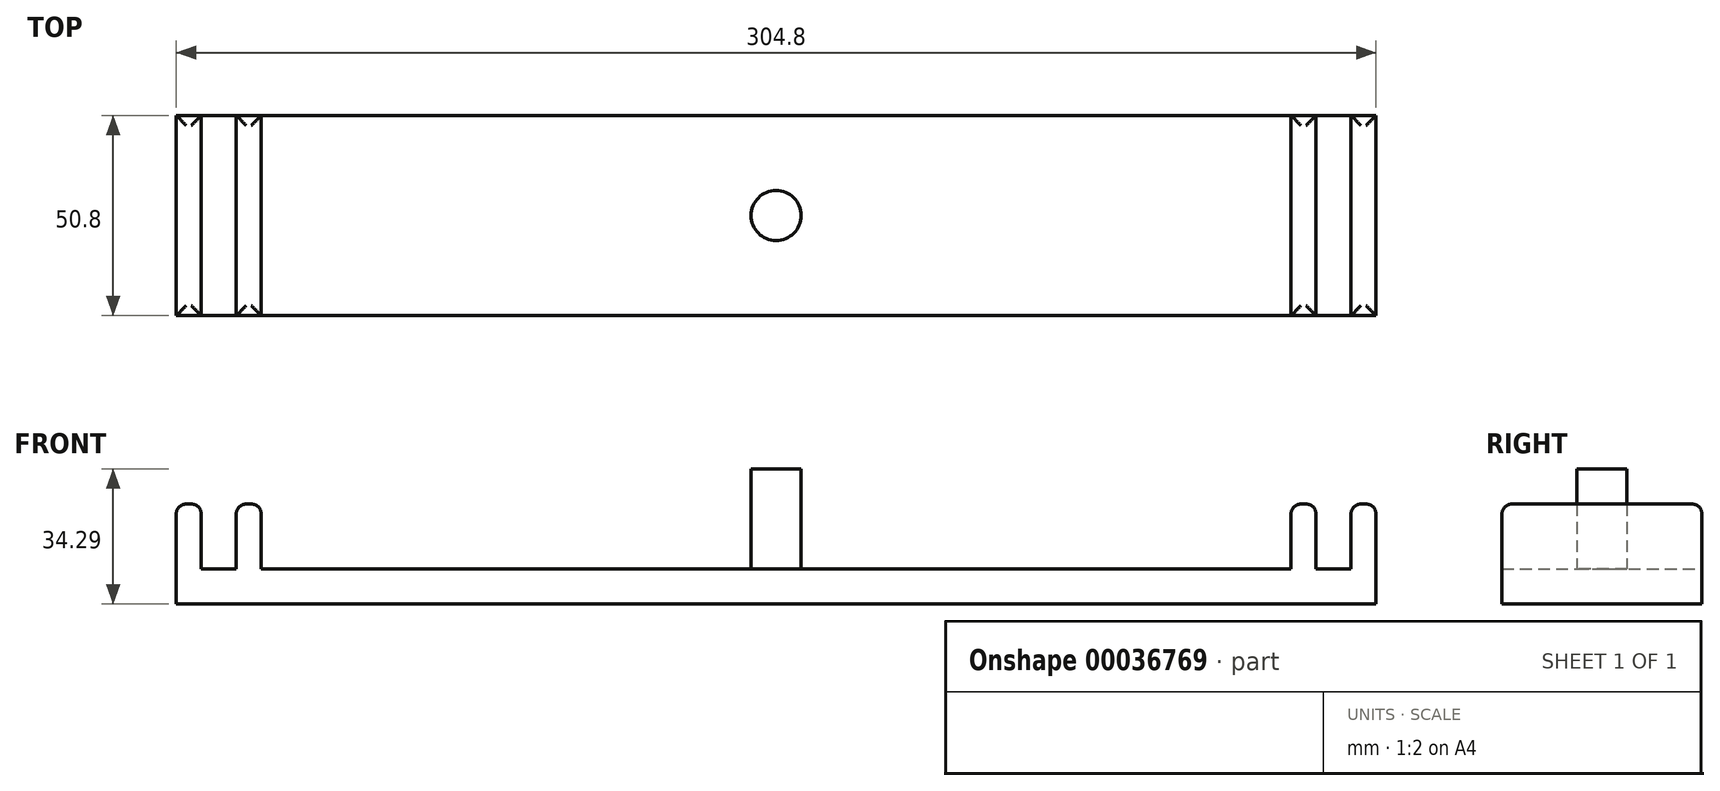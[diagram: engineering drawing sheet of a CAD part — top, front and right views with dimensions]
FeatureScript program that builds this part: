
annotation { "Feature Type Name" : "Feature", "Feature Type Description" : "" }
export const myFeature = defineFeature(function(context is Context, id is Id, definition is map)
    precondition{}
    {
        {
            var Q0;
            Q0=qCreatedBy(makeId("Front.planeOp"),FACE);
            var sketch = newSketch(context, id + "F0", { "sketchPlane" : qUnion([Q0])});
            skLineSegment(sketch, "E0", {"start": v(-152.4, 0) * mm, "end": v(0, 0) * mm});
            skLineSegment(sketch, "E1", {"start": v(-152.4, 0) * mm, "end": v(-152.4, 25.4) * mm});
            skLineSegment(sketch, "E2", {"start": v(-152.4, 25.4) * mm, "end": v(-146.05, 25.4) * mm});
            skLineSegment(sketch, "E3", {"start": v(-146.05, 25.4) * mm, "end": v(-146.05, 8.89) * mm});
            skLineSegment(sketch, "E4", {"start": v(-146.05, 8.89) * mm, "end": v(-137.16, 8.89) * mm});
            skLineSegment(sketch, "E5", {"start": v(-137.16, 8.89) * mm, "end": v(-137.16, 25.4) * mm});
            skLineSegment(sketch, "E6", {"start": v(-137.16, 25.4) * mm, "end": v(-130.8, 25.4) * mm});
            skLineSegment(sketch, "E7", {"start": v(-130.8, 25.4) * mm, "end": v(-130.8, 8.89) * mm});
            skLineSegment(sketch, "E8", {"start": v(-130.8, 8.89) * mm, "end": v(0, 8.9) * mm});
            skLineSegment(sketch, "E9.MirrorCS", {"start": v(152.4, 25.4) * mm, "end": v(146.05, 25.4) * mm});
            skLineSegment(sketch, "E10.MirrorCS", {"start": v(137.16, 25.4) * mm, "end": v(130.8, 25.4) * mm});
            skLineSegment(sketch, "E11.MirrorCS", {"start": v(152.4, 0) * mm, "end": v(0, 0) * mm});
            skLineSegment(sketch, "E12.MirrorCS", {"start": v(152.4, 0) * mm, "end": v(152.4, 25.4) * mm});
            skLineSegment(sketch, "E13.MirrorCS", {"start": v(137.16, 8.89) * mm, "end": v(137.16, 25.4) * mm});
            skLineSegment(sketch, "E14.MirrorCS", {"start": v(146.05, 25.4) * mm, "end": v(146.05, 8.89) * mm});
            skLineSegment(sketch, "E15.MirrorCS", {"start": v(146.05, 8.89) * mm, "end": v(137.16, 8.89) * mm});
            skLineSegment(sketch, "E16.MirrorCS", {"start": v(130.8, 8.89) * mm, "end": v(0, 8.9) * mm});
            skLineSegment(sketch, "E17.MirrorCS", {"start": v(130.8, 25.4) * mm, "end": v(130.8, 8.89) * mm});
            skSolve(sketch);
        }
        {
            var Q0;
            Q0 = qSketchRegion(id + "F0", true);
            extrude(context, id + "F1", {"entities" : qUnion([Q0]), "depth" : 50.8 * mm});
        }
        {
            var Q0;
            Q0=makeQuery(id+"F1.opExtrude","SWEPT_FACE",FACE,{"disambiguationData":[OSD([sQuery(id+"F0.wireOp",EDGE,"E2")])]});
            var Q1;
            Q1=makeQuery(id+"F1.opExtrude","SWEPT_FACE",FACE,{"disambiguationData":[OSD([sQuery(id+"F0.wireOp",EDGE,"E6")])]});
            var Q2;
            Q2=makeQuery(id+"F1.opExtrude","SWEPT_FACE",FACE,{"disambiguationData":[OSD([sQuery(id+"F0.wireOp",EDGE,"E10.MirrorCS")])]});
            var Q3;
            Q3=makeQuery(id+"F1.opExtrude","SWEPT_FACE",FACE,{"disambiguationData":[OSD([sQuery(id+"F0.wireOp",EDGE,"E9.MirrorCS")])]});
            fillet(context, id + "F2", {"entities" : qUnion([Q0, Q1, Q2, Q3]), "radius" : 2.54 * mm, "tangentPropagation" : true, "allowEdgeOverflow" : false});
        }
        {
            var Q0;
            Q0=makeQuery(id+"F1.opExtrude","SWEPT_FACE",FACE,{"disambiguationData":[OSD([sQuery(id+"F0.wireOp",EDGE,"E8"),sQuery(id+"F0.wireOp",EDGE,"E16.MirrorCS")])]});
            var sketch = newSketch(context, id + "F3", { "sketchPlane" : qUnion([Q0])});
            skCircle(sketch, "E18", {"center": v(0, -25.4) * mm, "radius": 6.35 * mm});
            skSolve(sketch);
        }
        {
            var Q0;
            Q0 = qSketchRegion(id + "F3", true);
            extrude(context, id + "F4", {"entities" : qUnion([Q0]), "operationType" : NewBodyOperationType.ADD, "depth" : 25.4 * mm});
        }
    });
